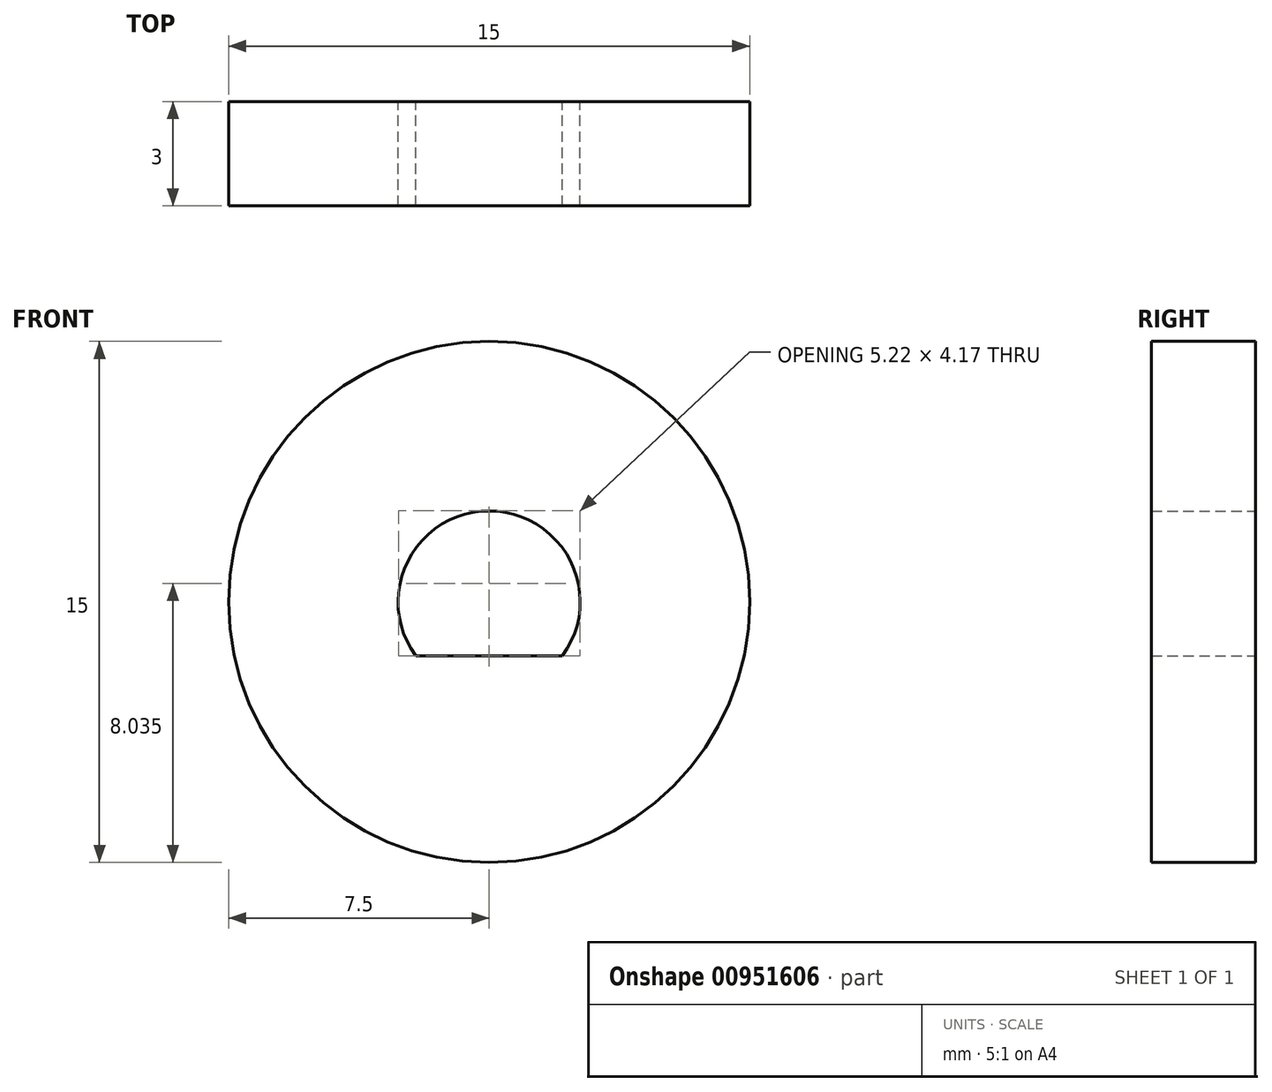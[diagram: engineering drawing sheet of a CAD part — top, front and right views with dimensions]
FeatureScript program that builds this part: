
annotation { "Feature Type Name" : "Feature", "Feature Type Description" : "" }
export const myFeature = defineFeature(function(context is Context, id is Id, definition is map)
    precondition{}
    {
        {
            var Q0;
            Q0=qCreatedBy(makeId("Front.planeOp"),FACE);
            var sketch = newSketch(context, id + "F0", { "sketchPlane" : qUnion([Q0])});
            skCircle(sketch, "E0", {"center": v(0, 0) * mm, "radius": 7.5 * mm});
            skLineSegment(sketch, "E1", {"start": v(0, 2.62) * mm, "end": v(0, -1.55) * mm, "construction": true});
            skLineSegment(sketch, "E2", {"start": v(0, -1.55) * mm, "end": v(2.11, -1.55) * mm});
            skLineSegment(sketch, "E3.MirrorCS", {"start": v(0, -1.55) * mm, "end": v(-2.11, -1.55) * mm});
            skArc(sketch, "E4", {"start": v(2.11, -1.55) * mm, "mid": v(0, 2.62) * mm, "end": v(-2.11, -1.55) * mm});
            skPoint(sketch, "E5", {"position": v(0, 2.62) * mm});
            skSolve(sketch);
        }
        {
            var Q0;
            Q0=qSketchRegion(id+"F0",true);
            extrude(context, id + "F1", {"entities" : qUnion([Q0]), "depth" : 3 * mm, "offsetDistance" : 25 * mm});
        }
    });
